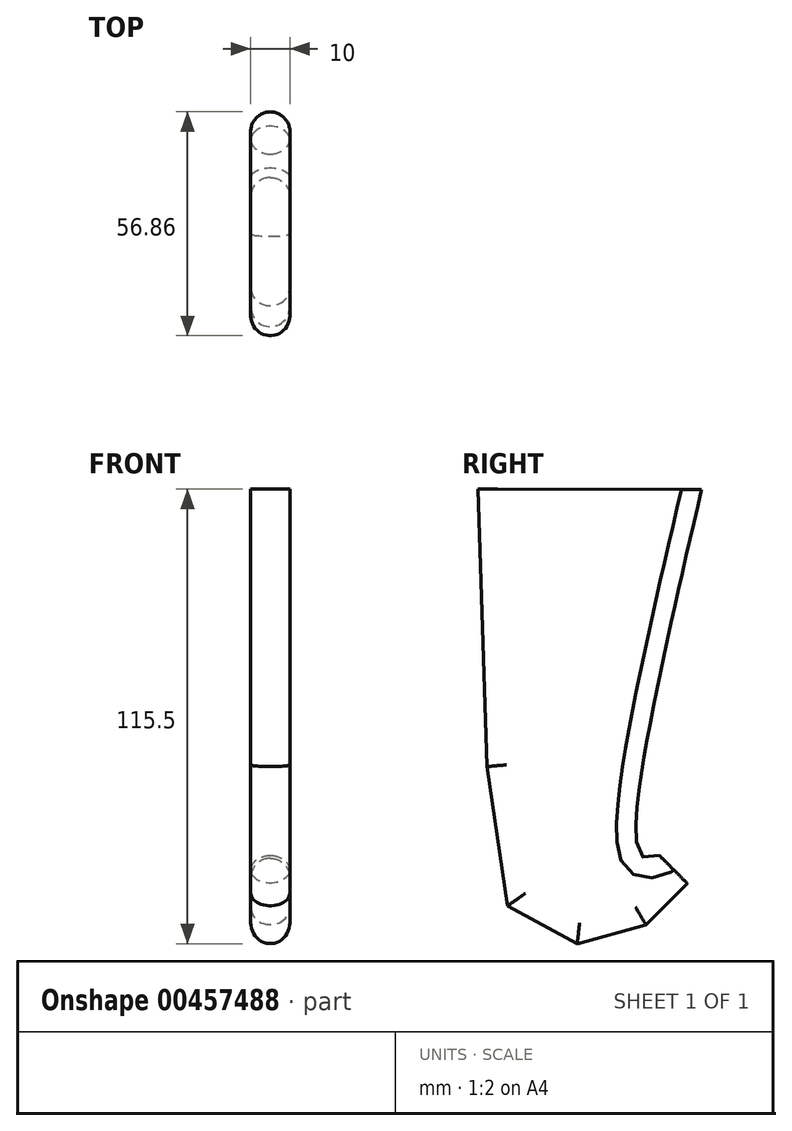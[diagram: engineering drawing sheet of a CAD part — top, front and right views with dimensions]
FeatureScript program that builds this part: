
annotation { "Feature Type Name" : "Feature", "Feature Type Description" : "" }
export const myFeature = defineFeature(function(context is Context, id is Id, definition is map)
    precondition{}
    {
        {
            var Q0;
            Q0=qCreatedBy(makeId("Top.planeOp"),FACE);
            var sketch = newSketch(context, id + "F0", { "sketchPlane" : qUnion([Q0])});
            skLineSegment(sketch, "E0.bottom", {"start": v(50, 50) * mm, "end": v(-50, 50) * mm});
            skLineSegment(sketch, "E0.top", {"start": v(50, -50) * mm, "end": v(-50, -50) * mm});
            skLineSegment(sketch, "E0.left", {"start": v(50, 50) * mm, "end": v(50, -50) * mm});
            skLineSegment(sketch, "E0.right", {"start": v(-50, 50) * mm, "end": v(-50, -50) * mm});
            skPoint(sketch, "E0.middle", {"position": v(0, 0) * mm});
            skSolve(sketch);
        }
        {
            var Q0;
            Q0=qCreatedBy(makeId("Right.planeOp"),FACE);
            var sketch = newSketch(context, id + "F1", { "sketchPlane" : qUnion([Q0])});
            skLineSegment(sketch, "E1", {"start": v(32.93, -92.93) * mm, "end": v(40, -100) * mm});
            skLineSegment(sketch, "E2", {"start": v(40, -100) * mm, "end": v(50, -100) * mm});
            skLineSegment(sketch, "E3", {"start": v(50, -100) * mm, "end": v(50, 0) * mm});
            skLineSegment(sketch, "E4", {"start": v(40, -100) * mm, "end": v(29.49, -110.51) * mm});
            skLineSegment(sketch, "E5", {"start": v(29.49, -110.51) * mm, "end": v(12.06, -115.35) * mm});
            skLineSegment(sketch, "E6", {"start": v(12.06, -115.35) * mm, "end": v(-5.63, -105.7) * mm});
            skLineSegment(sketch, "E7", {"start": v(-5.63, -105.7) * mm, "end": v(-10.9, -70.34) * mm});
            skLineSegment(sketch, "E8", {"start": v(-10.9, -70.34) * mm, "end": v(-13.2, 0.15) * mm});
            skFitSpline(sketch, "E9", {"points": [v(32.93, -92.93) * mm, v(28.21, -92.93) * mm, v(43.66, 0.05) * mm], "startDerivative": vector(-29.89, -10.4) * mm, "endDerivative": vector(37.17, 160.27) * mm});
            skLineSegment(sketch, "E10", {"start": v(43.66, 0.05) * mm, "end": v(-13.2, 0.15) * mm});
            skSolve(sketch);
        }
        {
            var Q0;
            Q0=makeQuery(id+"F1.imprint","IMPRINT",FACE,{"disambiguationData":[TD([[makeQuery(id+"F1.imprint","IMPRINT",EDGE,{"derivedFrom":sQuery(id+"F1.wireOp",EDGE,"E1")}),-1.0]])]});
            extrude(context, id + "F2", {"entities" : qUnion([Q0]), "endBound" : BoundingType.SYMMETRIC, "depth" : 10 * mm});
        }
        {
            var Q0;
            Q0=makeQuery(id+"F2.opExtrude","CAP_EDGE",EDGE,{"disambiguationData":[OSD([sQuery(id+"F1.wireOp",EDGE,"E9")])],"isStart":false});
            var Q1;
            Q1=makeQuery(id+"F2.opExtrude","CAP_EDGE",EDGE,{"disambiguationData":[OSD([sQuery(id+"F1.wireOp",EDGE,"E7")])],"isStart":false});
            var Q2;
            Q2=makeQuery(id+"F2.opExtrude","CAP_EDGE",EDGE,{"disambiguationData":[OSD([sQuery(id+"F1.wireOp",EDGE,"E6")])],"isStart":false});
            var Q3;
            Q3=makeQuery(id+"F2.opExtrude","CAP_EDGE",EDGE,{"disambiguationData":[OSD([sQuery(id+"F1.wireOp",EDGE,"E5")])],"isStart":false});
            var Q4;
            Q4=makeQuery(id+"F2.opExtrude","CAP_EDGE",EDGE,{"disambiguationData":[OSD([sQuery(id+"F1.wireOp",EDGE,"E4")])],"isStart":false});
            var Q5;
            Q5=makeQuery(id+"F2.opExtrude","CAP_EDGE",EDGE,{"disambiguationData":[OSD([sQuery(id+"F1.wireOp",EDGE,"E8")])],"isStart":false});
            var Q6;
            Q6=makeQuery(id+"F2.opExtrude","CAP_EDGE",EDGE,{"disambiguationData":[OSD([sQuery(id+"F1.wireOp",EDGE,"E8")])],"isStart":true});
            var Q7;
            Q7=makeQuery(id+"F2.opExtrude","CAP_EDGE",EDGE,{"disambiguationData":[OSD([sQuery(id+"F1.wireOp",EDGE,"E9")])],"isStart":true});
            var Q8;
            Q8=makeQuery(id+"F2.opExtrude","CAP_EDGE",EDGE,{"disambiguationData":[OSD([sQuery(id+"F1.wireOp",EDGE,"E4")])],"isStart":true});
            var Q9;
            Q9=makeQuery(id+"F2.opExtrude","CAP_EDGE",EDGE,{"disambiguationData":[OSD([sQuery(id+"F1.wireOp",EDGE,"E5")])],"isStart":true});
            var Q10;
            Q10=makeQuery(id+"F2.opExtrude","CAP_EDGE",EDGE,{"disambiguationData":[OSD([sQuery(id+"F1.wireOp",EDGE,"E6")])],"isStart":true});
            var Q11;
            Q11=makeQuery(id+"F2.opExtrude","CAP_EDGE",EDGE,{"disambiguationData":[OSD([sQuery(id+"F1.wireOp",EDGE,"E7")])],"isStart":true});
            fillet(context, id + "F3", {"entities" : qUnion([Q0, Q1, Q2, Q3, Q4, Q5, Q6, Q7, Q8, Q9, Q10, Q11]), "radius" : 5 * mm, "tangentPropagation" : true, "allowEdgeOverflow" : false});
        }
    });
